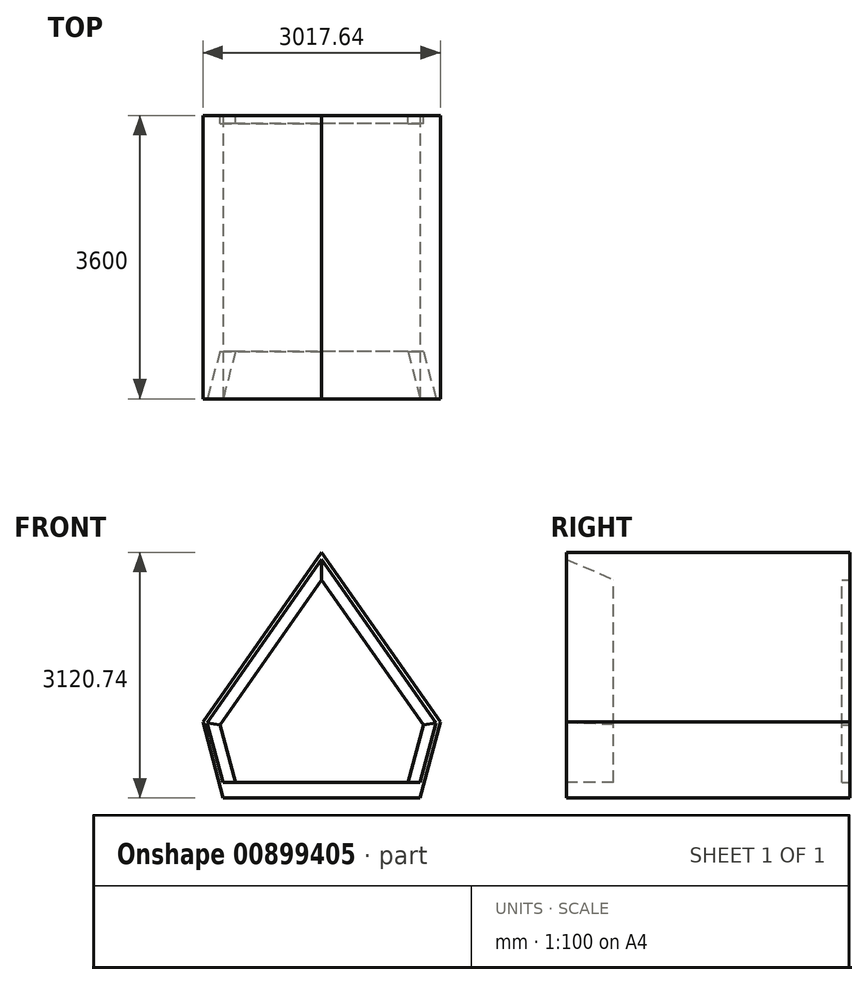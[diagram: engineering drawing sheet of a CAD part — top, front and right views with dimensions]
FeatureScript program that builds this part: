
annotation { "Feature Type Name" : "Feature", "Feature Type Description" : "" }
export const myFeature = defineFeature(function(context is Context, id is Id, definition is map)
    precondition{}
    {
        {
            var Q0;
            Q0=qCreatedBy(makeId("Front.planeOp"),FACE);
            var sketch = newSketch(context, id + "F0", { "sketchPlane" : qUnion([Q0])});
            skLineSegment(sketch, "E0", {"start": v(0, 0) * mm, "end": v(0, 3120.74) * mm, "construction": true});
            skLineSegment(sketch, "E1", {"start": v(0, 3120.74) * mm, "end": v(-1508.82, 965.93) * mm});
            skLineSegment(sketch, "E2", {"start": v(-1508.82, 965.93) * mm, "end": v(-1250, 0) * mm});
            skLineSegment(sketch, "E3", {"start": v(-1250, 0) * mm, "end": v(0, 0) * mm});
            skLineSegment(sketch, "E4.MirrorCS", {"start": v(1250, 0) * mm, "end": v(0, 0) * mm});
            skLineSegment(sketch, "E5.MirrorCS", {"start": v(0, 3120.74) * mm, "end": v(1508.82, 965.93) * mm});
            skLineSegment(sketch, "E6.MirrorCS", {"start": v(1508.82, 965.93) * mm, "end": v(1250, 0) * mm});
            skSolve(sketch);
        }
        {
            var Q0;
            Q0=makeQuery(id+"F0.imprint","IMPRINT",FACE,{"disambiguationData":[TD([[makeQuery(id+"F0.imprint","IMPRINT",EDGE,{"derivedFrom":sQuery(id+"F0.wireOp",EDGE,"E1")}),1.0]])]});
            extrude(context, id + "F1", {"entities" : qUnion([Q0]), "oppositeDirection" : true, "depth" : 3600 * mm, "offsetDistance" : 25 * mm});
        }
        {
            var Q0;
            Q0=makeQuery(id+"F1.opExtrude","CAP_FACE",FACE,{"disambiguationData":[OSD([sQuery(id+"F0.wireOp",EDGE,"E1"),sQuery(id+"F0.wireOp",EDGE,"E2"),sQuery(id+"F0.wireOp",EDGE,"E3"),sQuery(id+"F0.wireOp",EDGE,"E4.MirrorCS"),sQuery(id+"F0.wireOp",EDGE,"E5.MirrorCS"),sQuery(id+"F0.wireOp",EDGE,"E6.MirrorCS")])],"isStart":true});
            shell(context, id + "F2", {"entities" : qUnion([Q0]), "thickness" : 200 * mm});
        }
        {
            var Q0;
            Q0=makeQuery(id+"F1.opExtrude","CAP_FACE",FACE,{"disambiguationData":[OSD([sQuery(id+"F0.wireOp",EDGE,"E1"),sQuery(id+"F0.wireOp",EDGE,"E2"),sQuery(id+"F0.wireOp",EDGE,"E3"),sQuery(id+"F0.wireOp",EDGE,"E4.MirrorCS"),sQuery(id+"F0.wireOp",EDGE,"E5.MirrorCS"),sQuery(id+"F0.wireOp",EDGE,"E6.MirrorCS")])],"isStart":false});
            extrude(context, id + "F3", {"entities" : qUnion([Q0]), "operationType" : NewBodyOperationType.ADD, "oppositeDirection" : true, "depth" : 3000 * mm, "offsetDistance" : 25 * mm});
        }
        {
            var Q0;
            {var subQ0=sQuery(id+"F0.wireOp",EDGE,"E2");Q0=makeQuery(id+"F2.opShell","OFFSET_EDGE",EDGE,{"disambiguationData":[OSD([subQ0]),TDD([makeQuery(id+"F1.opExtrude","CAP_EDGE",EDGE,{"disambiguationData":[OSD([subQ0])],"isStart":true})])]});}
            var Q1;
            {var subQ0=sQuery(id+"F0.wireOp",EDGE,"E1");Q1=makeQuery(id+"F2.opShell","OFFSET_EDGE",EDGE,{"disambiguationData":[OSD([subQ0]),TDD([makeQuery(id+"F1.opExtrude","CAP_EDGE",EDGE,{"disambiguationData":[OSD([subQ0])],"isStart":true})])]});}
            var Q2;
            {var subQ0=sQuery(id+"F0.wireOp",EDGE,"E5.MirrorCS");Q2=makeQuery(id+"F2.opShell","OFFSET_EDGE",EDGE,{"disambiguationData":[OSD([subQ0]),TDD([makeQuery(id+"F1.opExtrude","CAP_EDGE",EDGE,{"disambiguationData":[OSD([subQ0])],"isStart":true})])]});}
            var Q3;
            {var subQ0=sQuery(id+"F0.wireOp",EDGE,"E6.MirrorCS");Q3=makeQuery(id+"F2.opShell","OFFSET_EDGE",EDGE,{"disambiguationData":[OSD([subQ0]),TDD([makeQuery(id+"F1.opExtrude","CAP_EDGE",EDGE,{"disambiguationData":[OSD([subQ0])],"isStart":true})])]});}
            chamfer(context, id + "F4", {"entities" : qUnion([Q0, Q1, Q2, Q3]), "chamferType" : ChamferType.TWO_OFFSETS, "width1" : 600 * mm, "oppositeDirection" : false, "width2" : 150 * mm, "tangentPropagation" : true});
        }
        {
            var Q0;
            Q0=makeQuery(id+"F1.opExtrude","CAP_FACE",FACE,{"disambiguationData":[OSD([sQuery(id+"F0.wireOp",EDGE,"E1"),sQuery(id+"F0.wireOp",EDGE,"E2"),sQuery(id+"F0.wireOp",EDGE,"E3"),sQuery(id+"F0.wireOp",EDGE,"E4.MirrorCS"),sQuery(id+"F0.wireOp",EDGE,"E5.MirrorCS"),sQuery(id+"F0.wireOp",EDGE,"E6.MirrorCS")])],"isStart":false});
            var sketch = newSketch(context, id + "F5", { "sketchPlane" : qUnion([Q0])});
            skLineSegment(sketch, "E7.0", {"start": v(-1291.5, 927.6) * mm, "end": v(0, 2772.05) * mm});
            skLineSegment(sketch, "E8.0", {"start": v(1291.5, 927.6) * mm, "end": v(0, 2772.05) * mm});
            skLineSegment(sketch, "E9.0", {"start": v(-1096.53, 200) * mm, "end": v(-1291.5, 927.6) * mm});
            skLineSegment(sketch, "E10.0", {"start": v(-1096.53, 200) * mm, "end": v(1096.53, 200) * mm});
            skLineSegment(sketch, "E11.0", {"start": v(1096.53, 200) * mm, "end": v(1291.5, 927.6) * mm});
            skSolve(sketch);
        }
        {
            var Q0;
            Q0=makeQuery(id+"F5.imprint","IMPRINT",FACE,{"disambiguationData":[TD([[makeQuery(id+"F5.imprint","IMPRINT",EDGE,{"derivedFrom":sQuery(id+"F5.wireOp",EDGE,"E7.0")}),-1.0]])]});
            extrude(context, id + "F6", {"entities" : qUnion([Q0]), "operationType" : NewBodyOperationType.REMOVE, "oppositeDirection" : true, "depth" : 100 * mm, "offsetDistance" : 25 * mm});
        }
    });
